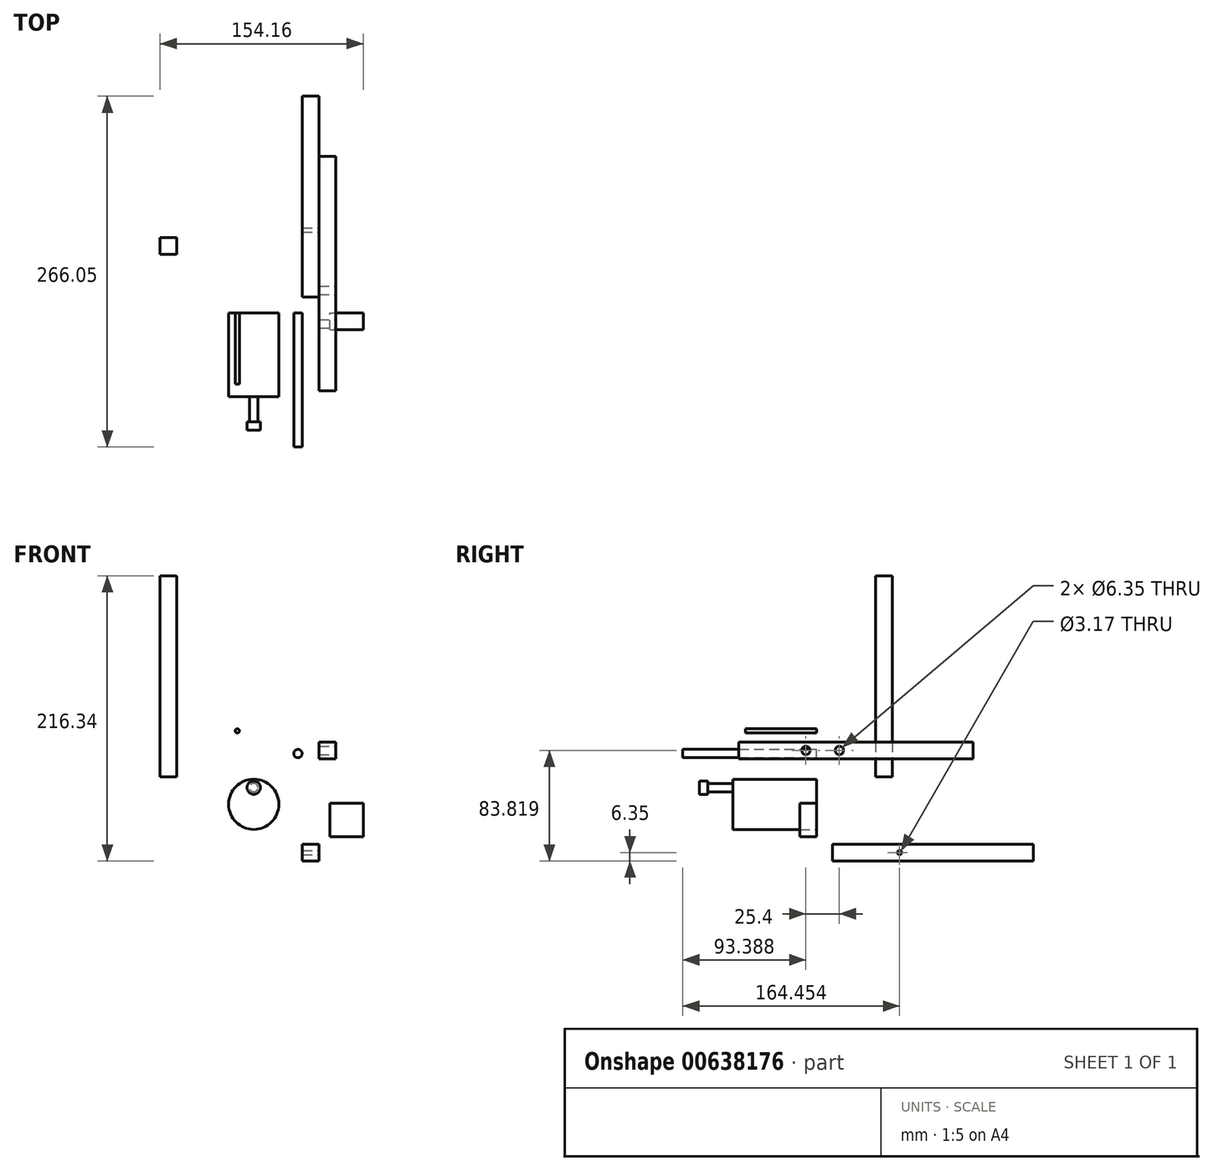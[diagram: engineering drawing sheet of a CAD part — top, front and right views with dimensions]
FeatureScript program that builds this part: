
annotation { "Feature Type Name" : "Feature", "Feature Type Description" : "" }
export const myFeature = defineFeature(function(context is Context, id is Id, definition is map)
    precondition{}
    {
        {
            var Q0;
            Q0=qCreatedBy(makeId("Right.planeOp"),FACE);
            var sketch = newSketch(context, id + "F0", { "sketchPlane" : qUnion([Q0])});
            skLineSegment(sketch, "E0.bottom", {"start": v(-59.01, 26.23) * mm, "end": v(118.79, 26.23) * mm});
            skLineSegment(sketch, "E0.top", {"start": v(-59.01, 13.53) * mm, "end": v(118.79, 13.53) * mm});
            skLineSegment(sketch, "E0.left", {"start": v(-59.01, 26.23) * mm, "end": v(-59.01, 13.53) * mm});
            skLineSegment(sketch, "E0.right", {"start": v(118.79, 26.23) * mm, "end": v(118.79, 13.53) * mm});
            skSolve(sketch);
        }
        {
            var Q0;
            Q0=makeQuery(id+"F0.imprint","IMPRINT",FACE,{"disambiguationData":[TD([[makeQuery(id+"F0.imprint","IMPRINT",EDGE,{"derivedFrom":sQuery(id+"F0.wireOp",EDGE,"E0.bottom")}),-1.0]])]});
            extrude(context, id + "F1", {"entities" : qUnion([Q0]), "depth" : 12.7 * mm, "offsetDistance" : 25.4 * mm});
        }
        {
            var Q0;
            Q0=makeQuery(id+"F1.opExtrude","CAP_FACE",FACE,{"disambiguationData":[OSD([sQuery(id+"F0.wireOp",EDGE,"E0.bottom"),sQuery(id+"F0.wireOp",EDGE,"E0.top"),sQuery(id+"F0.wireOp",EDGE,"E0.left"),sQuery(id+"F0.wireOp",EDGE,"E0.right")])],"isStart":false});
            var sketch = newSketch(context, id + "F2", { "sketchPlane" : qUnion([Q0])});
            skLineSegment(sketch, "E1", {"start": v(-59.01, 19.88) * mm, "end": v(-8.21, 19.88) * mm});
            skLineSegment(sketch, "E2", {"start": v(-8.21, 19.88) * mm, "end": v(17.19, 19.88) * mm});
            skCircle(sketch, "E3", {"center": v(-8.21, 19.88) * mm, "radius": 3.18 * mm});
            skCircle(sketch, "E4", {"center": v(17.19, 19.88) * mm, "radius": 3.18 * mm});
            skSolve(sketch);
        }
        {
            var Q0;
            {var subQ0=sQuery(id+"F2.wireOp",EDGE,"E2");var subQ1=sQuery(id+"F2.wireOp",EDGE,"E1");var subQ2=makeQuery(id+"F2.imprint","INTERSECT",VERTEX,{"derivedFrom":[subQ1,subQ0]});Q0=makeQuery(id+"F2.imprint","IMPRINT",FACE,{"disambiguationData":[TD([[makeQuery(id+"F2.imprint","IMPRINT",EDGE,{"disambiguationData":[TD([[subQ2,1.0]])],"derivedFrom":subQ1}),1.0]])]});}
            var Q1;
            {var subQ0=sQuery(id+"F2.wireOp",EDGE,"E2");var subQ1=sQuery(id+"F2.wireOp",EDGE,"E1");var subQ2=makeQuery(id+"F2.imprint","INTERSECT",VERTEX,{"derivedFrom":[subQ1,subQ0]});Q1=makeQuery(id+"F2.imprint","IMPRINT",FACE,{"disambiguationData":[TD([[makeQuery(id+"F2.imprint","IMPRINT",EDGE,{"disambiguationData":[TD([[subQ2,1.0]])],"derivedFrom":subQ1}),-1.0]])]});}
            var Q2;
            Q2=makeQuery(id+"F2.imprint","IMPRINT",FACE,{"disambiguationData":[TD([[makeQuery(id+"F2.imprint","IMPRINT",EDGE,{"derivedFrom":sQuery(id+"F2.wireOp",EDGE,"E4")}),1.0]])]});
            extrude(context, id + "F3", {"entities" : qUnion([Q0, Q1, Q2]), "operationType" : NewBodyOperationType.REMOVE, "oppositeDirection" : true, "depth" : 25.4 * mm, "offsetDistance" : 25.4 * mm});
        }
        {
            var Q0;
            Q0=qCreatedBy(makeId("Front.planeOp"),FACE);
            var sketch = newSketch(context, id + "F4", { "sketchPlane" : qUnion([Q0])});
            skCircle(sketch, "E5", {"center": v(-16.02, 17.51) * mm, "radius": 3.18 * mm});
            skSolve(sketch);
        }
        {
            var Q0;
            Q0=makeQuery(id+"F4.imprint","IMPRINT",FACE,{"disambiguationData":[TD([[makeQuery(id+"F4.imprint","IMPRINT",EDGE,{"derivedFrom":sQuery(id+"F4.wireOp",EDGE,"E5")}),1.0]])]});
            extrude(context, id + "F5", {"entities" : qUnion([Q0]), "depth" : 101.6 * mm, "offsetDistance" : 25.4 * mm});
        }
        {
            var Q0;
            Q0=qCreatedBy(makeId("Front.planeOp"),FACE);
            var sketch = newSketch(context, id + "F6", { "sketchPlane" : qUnion([Q0])});
            skCircle(sketch, "E6", {"center": v(-49.55, -21) * mm, "radius": 19.05 * mm});
            skSolve(sketch);
        }
        {
            var Q0;
            Q0=makeQuery(id+"F6.imprint","IMPRINT",FACE,{"disambiguationData":[TD([[makeQuery(id+"F6.imprint","IMPRINT",EDGE,{"derivedFrom":sQuery(id+"F6.wireOp",EDGE,"E6")}),1.0]])]});
            extrude(context, id + "F7", {"entities" : qUnion([Q0]), "depth" : 63.5 * mm, "offsetDistance" : 25.4 * mm});
        }
        {
            var Q0;
            Q0=makeQuery(id+"F7.opExtrude","CAP_FACE",FACE,{"disambiguationData":[OSD([sQuery(id+"F6.wireOp",EDGE,"E6")])],"isStart":false});
            var sketch = newSketch(context, id + "F8", { "sketchPlane" : qUnion([Q0])});
            skCircle(sketch, "E7", {"center": v(-49.55, -8.3) * mm, "radius": 3.18 * mm});
            skLineSegment(sketch, "E8", {"start": v(-49.55, -8.3) * mm, "end": v(-49.55, -1.95) * mm});
            skSolve(sketch);
        }
        {
            var Q0;
            Q0=makeQuery(id+"F8.imprint","IMPRINT",FACE,{"disambiguationData":[TD([[makeQuery(id+"F8.imprint","IMPRINT",EDGE,{"derivedFrom":sQuery(id+"F8.wireOp",EDGE,"E7")}),1.0]])]});
            extrude(context, id + "F9", {"entities" : qUnion([Q0]), "operationType" : NewBodyOperationType.ADD, "depth" : 19.05 * mm, "offsetDistance" : 25.4 * mm});
        }
        {
            var Q0;
            Q0=makeQuery(id+"F9.opExtrude","CAP_FACE",FACE,{"disambiguationData":[OSD([sQuery(id+"F8.wireOp",EDGE,"E7")])],"isStart":false});
            var sketch = newSketch(context, id + "F10", { "sketchPlane" : qUnion([Q0])});
            skCircle(sketch, "E9", {"center": v(-49.55, -8.3) * mm, "radius": 5.08 * mm});
            skSolve(sketch);
        }
        {
            var Q0;
            Q0=makeQuery(id+"F10.imprint","IMPRINT",FACE,{"disambiguationData":[TD([[makeQuery(id+"F10.imprint","IMPRINT",EDGE,{"derivedFrom":sQuery(id+"F10.wireOp",EDGE,"E9")}),1.0]])]});
            var Q1;
            Q1=makeQuery(id+"F10.imprint","IMPRINT",FACE,{"disambiguationData":[TD([[makeQuery(id+"F10.imprint","IMPRINT",EDGE,{"derivedFrom":makeQuery(id+"F9.opExtrude","CAP_EDGE",EDGE,{"disambiguationData":[OSD([sQuery(id+"F8.wireOp",EDGE,"E7")])],"isStart":false})}),1.0]])]});
            extrude(context, id + "F11", {"entities" : qUnion([Q0, Q1]), "operationType" : NewBodyOperationType.ADD, "depth" : 6.35 * mm, "offsetDistance" : 25.4 * mm});
        }
        {
            var Q0;
            Q0=qCreatedBy(makeId("Top.planeOp"),FACE);
            var sketch = newSketch(context, id + "F12", { "sketchPlane" : qUnion([Q0])});
            skLineSegment(sketch, "E10.bottom", {"start": v(-120.6, 57.42) * mm, "end": v(-107.9, 57.42) * mm});
            skLineSegment(sketch, "E10.top", {"start": v(-120.6, 44.72) * mm, "end": v(-107.9, 44.72) * mm});
            skLineSegment(sketch, "E10.left", {"start": v(-120.6, 57.42) * mm, "end": v(-120.6, 44.72) * mm});
            skLineSegment(sketch, "E10.right", {"start": v(-107.9, 57.42) * mm, "end": v(-107.9, 44.72) * mm});
            skSolve(sketch);
        }
        {
            var Q0;
            Q0=makeQuery(id+"F12.imprint","IMPRINT",FACE,{"disambiguationData":[TD([[makeQuery(id+"F12.imprint","IMPRINT",EDGE,{"derivedFrom":sQuery(id+"F12.wireOp",EDGE,"E10.bottom")}),-1.0]])]});
            extrude(context, id + "F13", {"entities" : qUnion([Q0]), "depth" : 152.4 * mm, "offsetDistance" : 25.4 * mm});
        }
        {
            var Q0;
            Q0=qCreatedBy(makeId("Right.planeOp"),FACE);
            var sketch = newSketch(context, id + "F14", { "sketchPlane" : qUnion([Q0])});
            skLineSegment(sketch, "E11.bottom", {"start": v(12.05, -63.94) * mm, "end": v(164.45, -63.94) * mm});
            skLineSegment(sketch, "E11.top", {"start": v(12.05, -51.24) * mm, "end": v(164.45, -51.24) * mm});
            skLineSegment(sketch, "E11.left", {"start": v(12.05, -63.94) * mm, "end": v(12.05, -51.24) * mm});
            skLineSegment(sketch, "E11.right", {"start": v(164.45, -63.94) * mm, "end": v(164.45, -51.24) * mm});
            skSolve(sketch);
        }
        {
            var Q0;
            Q0=makeQuery(id+"F14.imprint","IMPRINT",FACE,{"disambiguationData":[TD([[makeQuery(id+"F14.imprint","IMPRINT",EDGE,{"derivedFrom":sQuery(id+"F14.wireOp",EDGE,"E11.bottom")}),1.0]])]});
            extrude(context, id + "F15", {"entities" : qUnion([Q0]), "oppositeDirection" : true, "depth" : 12.7 * mm, "offsetDistance" : 25.4 * mm});
        }
        {
            var Q0;
            Q0=makeQuery(id+"F15.opExtrude","CAP_FACE",FACE,{"disambiguationData":[OSD([sQuery(id+"F14.wireOp",EDGE,"E11.bottom"),sQuery(id+"F14.wireOp",EDGE,"E11.top"),sQuery(id+"F14.wireOp",EDGE,"E11.left"),sQuery(id+"F14.wireOp",EDGE,"E11.right")])],"isStart":true});
            var sketch = newSketch(context, id + "F16", { "sketchPlane" : qUnion([Q0])});
            skLineSegment(sketch, "E12", {"start": v(12.05, -57.6) * mm, "end": v(62.85, -57.6) * mm});
            skCircle(sketch, "E13", {"center": v(62.85, -57.6) * mm, "radius": 1.59 * mm});
            skSolve(sketch);
        }
        {
            var Q0;
            Q0=makeQuery(id+"F16.imprint","IMPRINT",FACE,{"disambiguationData":[TD([[makeQuery(id+"F16.imprint","IMPRINT",EDGE,{"derivedFrom":sQuery(id+"F16.wireOp",EDGE,"E13")}),1.0]])]});
            extrude(context, id + "F17", {"entities" : qUnion([Q0]), "operationType" : NewBodyOperationType.REMOVE, "oppositeDirection" : true, "depth" : 25.4 * mm, "offsetDistance" : 25.4 * mm});
        }
        {
            var Q0;
            Q0=qCreatedBy(makeId("Front.planeOp"),FACE);
            var sketch = newSketch(context, id + "F18", { "sketchPlane" : qUnion([Q0])});
            skCircle(sketch, "E14", {"center": v(-62.07, 34.68) * mm, "radius": 1.59 * mm});
            skSolve(sketch);
        }
        {
            var Q0;
            Q0=makeQuery(id+"F18.imprint","IMPRINT",FACE,{"disambiguationData":[TD([[makeQuery(id+"F18.imprint","IMPRINT",EDGE,{"derivedFrom":sQuery(id+"F18.wireOp",EDGE,"E14")}),1.0]])]});
            extrude(context, id + "F19", {"entities" : qUnion([Q0]), "depth" : 53.97 * mm, "offsetDistance" : 25.4 * mm});
        }
        {
            var Q0;
            Q0=qCreatedBy(makeId("Front.planeOp"),FACE);
            var sketch = newSketch(context, id + "F20", { "sketchPlane" : qUnion([Q0])});
            skLineSegment(sketch, "E15.bottom", {"start": v(8.16, -20.22) * mm, "end": v(33.56, -20.22) * mm});
            skLineSegment(sketch, "E15.top", {"start": v(8.16, -45.62) * mm, "end": v(33.56, -45.62) * mm});
            skLineSegment(sketch, "E15.left", {"start": v(8.16, -20.22) * mm, "end": v(8.16, -45.62) * mm});
            skLineSegment(sketch, "E15.right", {"start": v(33.56, -20.22) * mm, "end": v(33.56, -45.62) * mm});
            skSolve(sketch);
        }
        {
            var Q0;
            Q0=makeQuery(id+"F20.imprint","IMPRINT",FACE,{"disambiguationData":[TD([[makeQuery(id+"F20.imprint","IMPRINT",EDGE,{"derivedFrom":sQuery(id+"F20.wireOp",EDGE,"E15.bottom")}),-1.0]])]});
            extrude(context, id + "F21", {"entities" : qUnion([Q0]), "depth" : 12.7 * mm, "offsetDistance" : 25.4 * mm});
        }
    });
